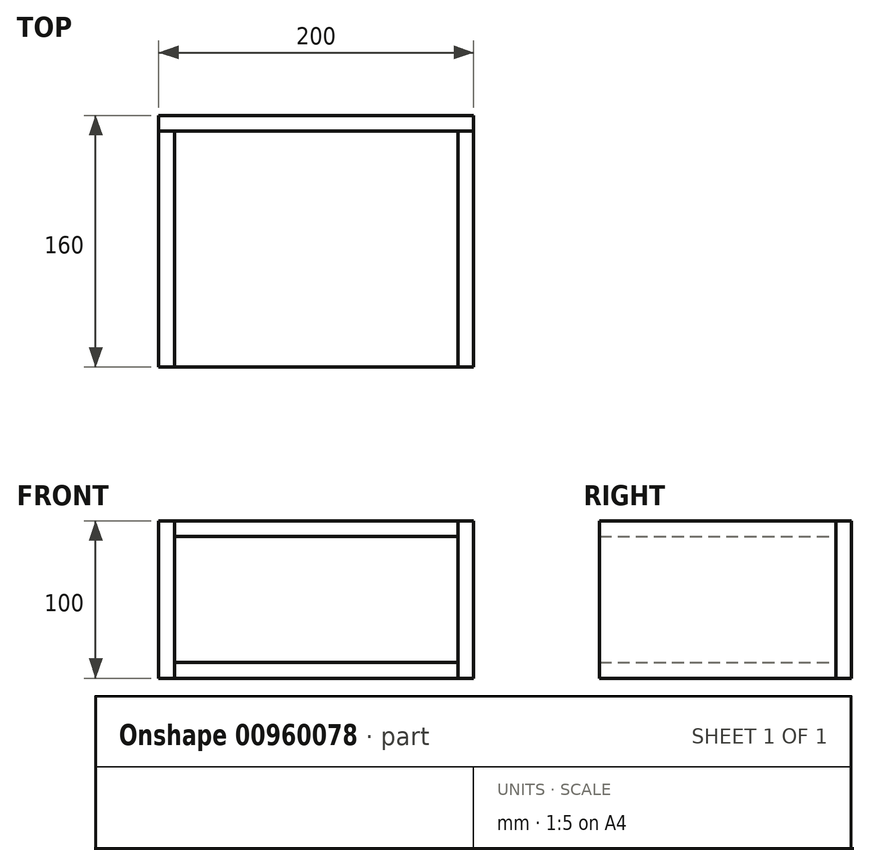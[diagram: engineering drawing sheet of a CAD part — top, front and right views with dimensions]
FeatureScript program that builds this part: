
annotation { "Feature Type Name" : "Feature", "Feature Type Description" : "" }
export const myFeature = defineFeature(function(context is Context, id is Id, definition is map)
    precondition{}
    {
        {
            var Q0;
            Q0=qCreatedBy(makeId("Front.planeOp"),FACE);
            var sketch = newSketch(context, id + "F0", { "sketchPlane" : qUnion([Q0])});
            skLineSegment(sketch, "E0.bottom", {"start": v(-100, -50) * mm, "end": v(100, -50) * mm});
            skLineSegment(sketch, "E0.top", {"start": v(-100, 50) * mm, "end": v(100, 50) * mm});
            skLineSegment(sketch, "E0.left", {"start": v(-100, -50) * mm, "end": v(-100, 50) * mm});
            skLineSegment(sketch, "E0.right", {"start": v(100, -50) * mm, "end": v(100, 50) * mm});
            skPoint(sketch, "E0.middle", {"position": v(0, 0) * mm});
            skSolve(sketch);
        }
        {
            var Q0;
            Q0=makeQuery(id+"F0.imprint","IMPRINT",FACE,{"disambiguationData":[TD([[makeQuery(id+"F0.imprint","IMPRINT",EDGE,{"derivedFrom":sQuery(id+"F0.wireOp",EDGE,"E0.bottom")}),1.0]])]});
            extrude(context, id + "F1", {"entities" : qUnion([Q0]), "depth" : 10 * mm, "offsetDistance" : 25 * mm});
        }
        {
            var Q0;
            Q0=makeQuery(id+"F1.opExtrude","CAP_FACE",FACE,{"disambiguationData":[OSD([sQuery(id+"F0.wireOp",EDGE,"E0.bottom"),sQuery(id+"F0.wireOp",EDGE,"E0.top"),sQuery(id+"F0.wireOp",EDGE,"E0.left"),sQuery(id+"F0.wireOp",EDGE,"E0.right")])],"isStart":false});
            var sketch = newSketch(context, id + "F2", { "sketchPlane" : qUnion([Q0])});
            skLineSegment(sketch, "E1.bottom", {"start": v(-100, 50) * mm, "end": v(-90, 50) * mm});
            skLineSegment(sketch, "E1.top", {"start": v(-100, -50) * mm, "end": v(-90, -50) * mm});
            skLineSegment(sketch, "E1.left", {"start": v(-100, 50) * mm, "end": v(-100, -50) * mm});
            skLineSegment(sketch, "E1.right", {"start": v(-90, 50) * mm, "end": v(-90, -50) * mm});
            skSolve(sketch);
        }
        {
            var Q0;
            Q0 = qSketchRegion(id + "F2", true);
            extrude(context, id + "F3", {"entities" : qUnion([Q0]), "depth" : 150 * mm, "offsetDistance" : 25 * mm});
        }
        {
            var Q0;
            Q0=makeQuery(id+"F3.opExtrude","SWEPT_BODY",BODY,{"disambiguationData":[OSD([sQuery(id+"F2.wireOp",EDGE,"E1.bottom"),sQuery(id+"F2.wireOp",EDGE,"E1.top"),sQuery(id+"F2.wireOp",EDGE,"E1.left"),sQuery(id+"F2.wireOp",EDGE,"E1.right")])]});
            var Q1;
            Q1=qCreatedBy(makeId("Right.planeOp"),FACE);
            mirror(context, id + "F4", {"entities" : qUnion([Q0]), "mirrorPlane" : qUnion([Q1])});
        }
        {
            var Q0;
            Q0=makeQuery(id+"F3.opExtrude","SWEPT_FACE",FACE,{"disambiguationData":[OSD([sQuery(id+"F2.wireOp",EDGE,"E1.bottom")])]});
            var sketch = newSketch(context, id + "F5", { "sketchPlane" : qUnion([Q0])});
            skLineSegment(sketch, "E2.bottom", {"start": v(-90, -10) * mm, "end": v(90, -10) * mm});
            skLineSegment(sketch, "E2.top", {"start": v(-90, -160) * mm, "end": v(90, -160) * mm});
            skLineSegment(sketch, "E2.left", {"start": v(-90, -10) * mm, "end": v(-90, -160) * mm});
            skLineSegment(sketch, "E2.right", {"start": v(90, -10) * mm, "end": v(90, -160) * mm});
            skSolve(sketch);
        }
        {
            var Q0;
            Q0=makeQuery(id+"F5.imprint","IMPRINT",FACE,{"disambiguationData":[TD([[makeQuery(id+"F5.imprint","IMPRINT",EDGE,{"derivedFrom":sQuery(id+"F5.wireOp",EDGE,"E2.bottom")}),-1.0]])]});
            extrude(context, id + "F6", {"entities" : qUnion([Q0]), "oppositeDirection" : true, "depth" : 10 * mm, "offsetDistance" : 25 * mm});
        }
        {
            var Q0;
            Q0=makeQuery(id+"F6.opExtrude","SWEPT_BODY",BODY,{"disambiguationData":[OSD([sQuery(id+"F5.wireOp",EDGE,"E2.bottom"),sQuery(id+"F5.wireOp",EDGE,"E2.top"),sQuery(id+"F5.wireOp",EDGE,"E2.left"),sQuery(id+"F5.wireOp",EDGE,"E2.right")])]});
            var Q1;
            Q1=qCreatedBy(makeId("Top.planeOp"),FACE);
            mirror(context, id + "F7", {"entities" : qUnion([Q0]), "mirrorPlane" : qUnion([Q1])});
        }
    });
